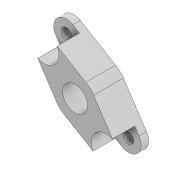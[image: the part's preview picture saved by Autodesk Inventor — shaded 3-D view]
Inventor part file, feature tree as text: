
AUTODESK INVENTOR PART (.ipt)
format: ipt  version: 2022 (Build 260153000, 153)  size: 159,232 bytes
history: native  units: mm
features: reference x6, sketch x4, extrude x3, other x2, hole x1, projected_geometry x1
ambient origin geometry x8: Origin, YZ Plane, XZ Plane, XY Plane, X Axis, Y Axis, Z Axis, Center Point
bodies: Volumenkörper1 (feature_tree)
feature tree (17):
  extrude  "Extrusion1"  Depth=2.0mm
  extrude  "Extrusion2"  Depth=6.7mm
  extrude  "Extrusion3"  [1 undecoded]
  hole  "Bohrung1"  [1 undecoded]
  sketch  "Skizze1"  dims[d0=8.0mm d1=0.0mm d2=2.0mm]
  reference  "Referenz1"
  reference  "Referenz2"
  reference  "Referenz3"
  sketch  "Skizze2"  dims[d3=3.0mm d4=0.0mm d5=6.7mm]
  projected_geometry  "Projizierte Kontur1"
  sketch  "Skizze3"  dims[d6=3.0mm d7=0.0mm]
  reference  "Referenz4"
  reference  "Referenz5"
  reference  "Referenz6"
  sketch  "Skizze4"  dims[d8=2.8mm d9=6.0mm d10=8.0mm d11=6.0mm d12=90.0deg d13=8.0mm d14=20.594885mm]
  other  "Assembly_Matchboxscope_injectionmolded.iam"
  other  "IM_Matchboxscope_base:1"
note: 2 required parameter values undecoded (feature->parameter linkage not recoverable at this tier; creation-order binding heuristic only, values carry confidence <= 0.55)
